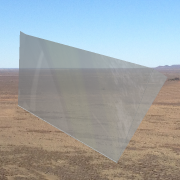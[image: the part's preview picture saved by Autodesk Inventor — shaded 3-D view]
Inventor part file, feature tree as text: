
AUTODESK INVENTOR PART (.ipt)
format: ipt  version: 2013 SP2 (Build 170200200, 200)  size: 204,800 bytes
history: native  units: in
note: dims shown in document units (in); Inventor stores cm internally (conversion verified against a paired STEP export)
features: extrude x5, sketch x5, plane x2, other x2, loft x1
ambient origin geometry x8: Origin, YZ Plane, XZ Plane, XY Plane, X Axis, Y Axis, Z Axis, Center Point
bodies: Solid1 (feature_tree)
feature tree (15):
  extrude  "Extrusion1"  Depth=1.0in
  plane  "Work Plane1"
  extrude  "Extrusion2"  Depth=0.0481in
  extrude  "Extrusion3"  Depth=0.25in
  plane  "Work Plane3"
  extrude  "Extrusion5"  Depth=7.0in
  extrude  "Extrusion6"  TaperAngle=60.0deg  [1 undecoded]
  loft  "Loft1"
  sketch  "Sketch1"  dims[d0=136.0in d1=1.0in]
  sketch  "Sketch2"  dims[d2=0.25in d3=0.0in d4=0.0481in]
  sketch  "Sketch3"  dims[d5=1.0in d6=0.25in]
  sketch  "Sketch5"  dims[d7=80.0in d8=0.0in d10=7.0in]
  sketch  "Sketch6"  dims[d11=0.25in d12=0.0in d17=60.0deg d18=1.0in d19=100.0in d20=0.25in d21=0.0in d22=20.0in d23=0.25in d24=0.0in d25=0.0in d26=90.0deg d27=0.0in d28=90.0deg]
  other  "Edges1"
  other  "Edges2"
note: 1 required parameter value undecoded (feature->parameter linkage not recoverable at this tier; creation-order binding heuristic only, values carry confidence <= 0.55)
